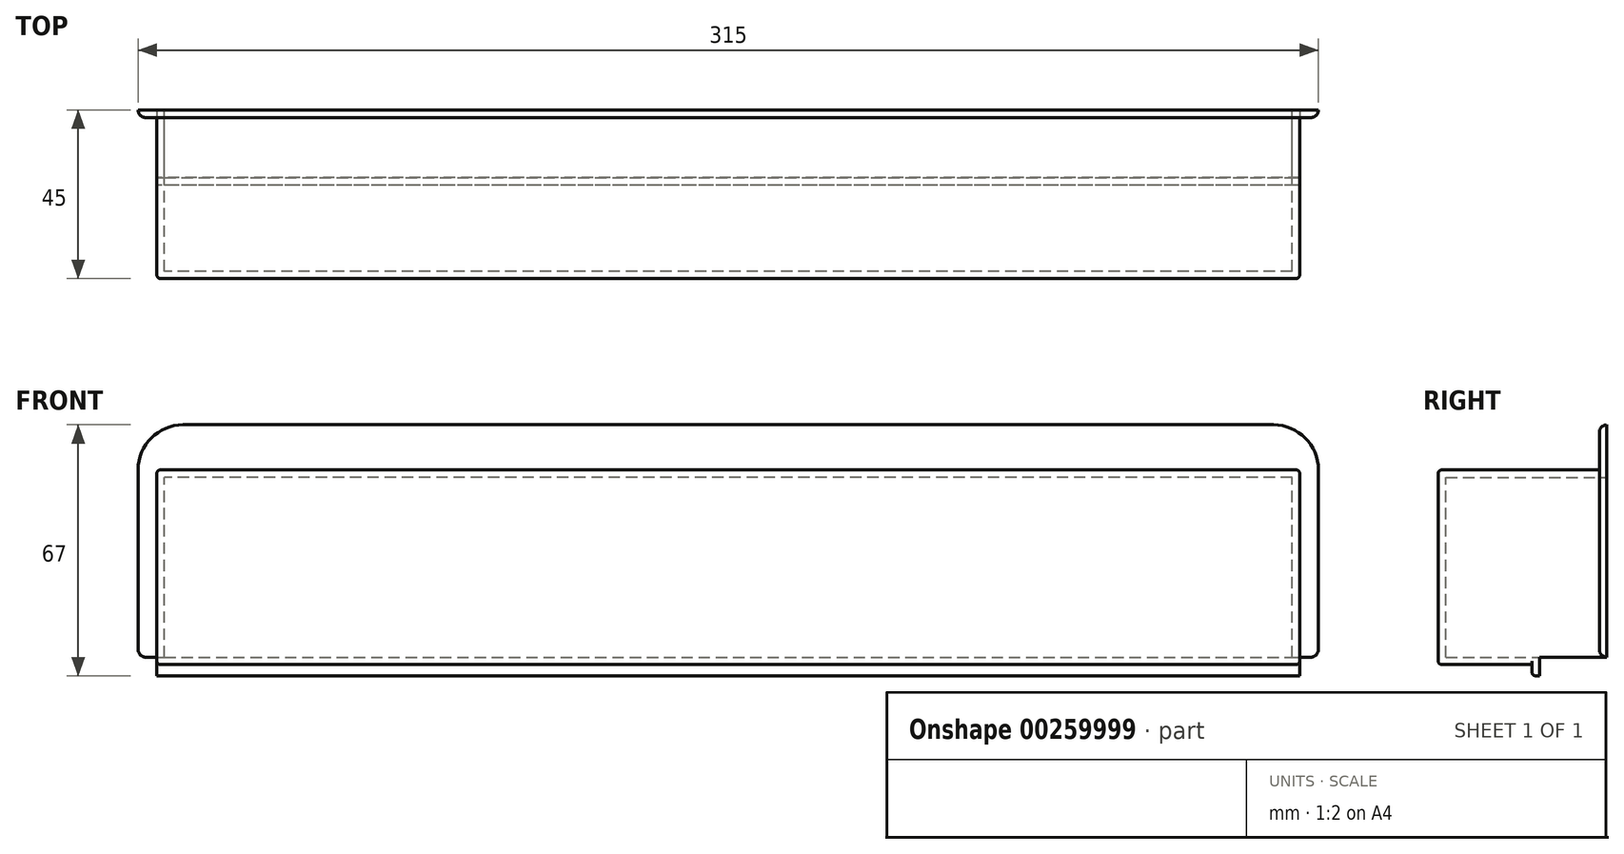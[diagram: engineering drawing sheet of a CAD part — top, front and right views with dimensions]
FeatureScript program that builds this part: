
annotation { "Feature Type Name" : "Feature", "Feature Type Description" : "" }
export const myFeature = defineFeature(function(context is Context, id is Id, definition is map)
    precondition{}
    {
        {
            var Q0;
            Q0=qCreatedBy(makeId("Front.planeOp"),FACE);
            cPlane(context, id + "F0", {"entities" : qUnion([Q0]), "cplaneType" : CPlaneType.OFFSET, "offset" : 15 * mm, "width" : 150 * mm, "height" : 150 * mm});
        }
        {
            var Q0;
            Q0=qCreatedBy(id+"F0.planeOp",FACE);
            var sketch = newSketch(context, id + "F1", { "sketchPlane" : qUnion([Q0])});
            skLineSegment(sketch, "E0.bottom", {"start": v(152.5, -26) * mm, "end": v(-152.5, -26) * mm});
            skLineSegment(sketch, "E0.top", {"start": v(152.5, 26) * mm, "end": v(-152.5, 26) * mm});
            skLineSegment(sketch, "E0.left", {"start": v(152.5, -26) * mm, "end": v(152.5, 26) * mm});
            skLineSegment(sketch, "E0.right", {"start": v(-152.5, -26) * mm, "end": v(-152.5, 26) * mm});
            skPoint(sketch, "E0.middle", {"position": v(0, 0) * mm});
            skLineSegment(sketch, "E1.bottom", {"start": v(150.5, -24) * mm, "end": v(-150.5, -24) * mm});
            skLineSegment(sketch, "E1.top", {"start": v(150.5, 24) * mm, "end": v(-150.5, 24) * mm});
            skLineSegment(sketch, "E1.left", {"start": v(150.5, -24) * mm, "end": v(150.5, 24) * mm});
            skLineSegment(sketch, "E1.right", {"start": v(-150.5, -24) * mm, "end": v(-150.5, 24) * mm});
            skLineSegment(sketch, "E2.top", {"start": v(152.5, 38) * mm, "end": v(-152.5, 38) * mm});
            skLineSegment(sketch, "E2.left", {"start": v(152.5, 26) * mm, "end": v(152.5, 38) * mm});
            skLineSegment(sketch, "E2.right", {"start": v(-152.5, 26) * mm, "end": v(-152.5, 38) * mm});
            skLineSegment(sketch, "E3.left", {"start": v(152.5, -26) * mm, "end": v(152.5, -26) * mm});
            skLineSegment(sketch, "E3.right", {"start": v(-152.5, -26) * mm, "end": v(-152.5, -26) * mm});
            skLineSegment(sketch, "E4.bottom", {"start": v(-152.5, 38) * mm, "end": v(-157.5, 38) * mm});
            skLineSegment(sketch, "E4.left", {"start": v(-152.5, 38) * mm, "end": v(-152.5, -26) * mm});
            skLineSegment(sketch, "E4.right", {"start": v(-157.5, 38) * mm, "end": v(-157.5, -24) * mm});
            skLineSegment(sketch, "E5.left", {"start": v(152.5, 38) * mm, "end": v(152.5, -26) * mm});
            skLineSegment(sketch, "E5.right", {"start": v(157.5, 38) * mm, "end": v(157.5, -24) * mm});
            skLineSegment(sketch, "E6", {"start": v(150.5, -24) * mm, "end": v(152.5, -24) * mm});
            skLineSegment(sketch, "E7", {"start": v(-150.5, -24) * mm, "end": v(-152.5, -24) * mm});
            skLineSegment(sketch, "E8", {"start": v(152.5, -24) * mm, "end": v(157.5, -24) * mm});
            skLineSegment(sketch, "E9", {"start": v(-152.5, -24) * mm, "end": v(-157.5, -24) * mm});
            skLineSegment(sketch, "E10", {"start": v(157.5, 38) * mm, "end": v(157.5, 38) * mm});
            skLineSegment(sketch, "E11", {"start": v(157.5, 38) * mm, "end": v(152.5, 38) * mm});
            skSolve(sketch);
        }
        {
            var Q0;
            Q0=makeQuery(id+"F1.imprint","IMPRINT",FACE,{"disambiguationData":[TD([[makeQuery(id+"F1.imprint","IMPRINT",EDGE,{"derivedFrom":sQuery(id+"F1.wireOp",EDGE,"E1.bottom")}),1.0]])]});
            var Q1;
            Q1=makeQuery(id+"F1.imprint","IMPRINT",FACE,{"disambiguationData":[TD([[makeQuery(id+"F1.imprint","IMPRINT",EDGE,{"derivedFrom":sQuery(id+"F1.wireOp",EDGE,"E1.top")}),-1.0]])]});
            extrude(context, id + "F2", {"entities" : qUnion([Q0, Q1]), "depth" : 45 * mm});
        }
        {
            var Q0;
            {var subQ0=sQuery(id+"F1.wireOp",EDGE,"E0.top");Q0=makeQuery(id+"F1.imprint","IMPRINT",FACE,{"disambiguationData":[TD([[makeQuery(id+"F1.imprint","IMPRINT",EDGE,{"derivedFrom":subQ0}),-1.0]])]});}
            var Q1;
            {var subQ4=sQuery(id+"F1.wireOp",EDGE,"E4.bottom");Q1=makeQuery(id+"F1.imprint","IMPRINT",FACE,{"disambiguationData":[TD([[makeQuery(id+"F1.imprint","IMPRINT",EDGE,{"derivedFrom":subQ4}),1.0]])]});}
            var Q2;
            {var subQ0=sQuery(id+"F1.wireOp",EDGE,"E0.bottom");Q2=makeQuery(id+"F1.imprint","IMPRINT",FACE,{"disambiguationData":[TD([[makeQuery(id+"F1.imprint","IMPRINT",EDGE,{"derivedFrom":subQ0}),1.0]])]});}
            var Q3;
            {var subQ3=sQuery(id+"F1.wireOp",EDGE,"E5.bottom");Q3=makeQuery(id+"F1.imprint","IMPRINT",FACE,{"disambiguationData":[TD([[makeQuery(id+"F1.imprint","IMPRINT",EDGE,{"derivedFrom":subQ3}),-1.0]])]});}
            extrude(context, id + "F3", {"entities" : qUnion([Q0, Q1, Q2, Q3]), "operationType" : NewBodyOperationType.ADD, "depth" : 2 * mm});
        }
        {
            var Q0;
            Q0=makeQuery(id+"F1.imprint","IMPRINT",FACE,{"disambiguationData":[TD([[makeQuery(id+"F1.imprint","IMPRINT",EDGE,{"derivedFrom":sQuery(id+"F1.wireOp",EDGE,"E1.bottom")}),-1.0]])]});
            extrude(context, id + "F4", {"entities" : qUnion([Q0]), "operationType" : NewBodyOperationType.ADD, "depth" : 45 * mm});
        }
        {
            var Q0;
            Q0=makeQuery(id+"F1.imprint","IMPRINT",FACE,{"disambiguationData":[TD([[makeQuery(id+"F1.imprint","IMPRINT",EDGE,{"derivedFrom":sQuery(id+"F1.wireOp",EDGE,"E1.bottom")}),-1.0]])]});
            extrude(context, id + "F5", {"entities" : qUnion([Q0]), "operationType" : NewBodyOperationType.REMOVE, "depth" : 43 * mm});
        }
        {
            var Q0;
            Q0=makeQuery(id+"F3.opExtrude","SWEPT_EDGE",EDGE,{"disambiguationData":[OSD([sQuery(id+"F1.wireOp",EDGE,"E4.bottom"),sQuery(id+"F1.wireOp",EDGE,"E4.right")])]});
            var Q1;
            Q1=makeQuery(id+"FlA18t3Lp9otsd1_1.opFillet","BLEND_EDGE",EDGE,{"blendedFrom":[makeQuery(id+"F3.opExtrude","CAP_EDGE",EDGE,{"disambiguationData":[OSD([sQuery(id+"F1.wireOp",EDGE,"E2.top"),sQuery(id+"F1.wireOp",EDGE,"E4.bottom"),sQuery(id+"F1.wireOp",EDGE,"E5.bottom")])],"isStart":false}),makeQuery(id+"F3.opExtrude","CAP_EDGE",EDGE,{"disambiguationData":[OSD([sQuery(id+"F1.wireOp",EDGE,"E5.right")])],"isStart":false})],"blendedInto":[]});
            fillet(context, id + "F6", {"entities" : qUnion([Q0, Q1]), "radius" : 5 * mm, "tangentPropagation" : true, "allowEdgeOverflow" : false});
        }
        {
            var Q0;
            Q0=makeQuery(id+"F1.imprint","IMPRINT",FACE,{"disambiguationData":[TD([[makeQuery(id+"F1.imprint","IMPRINT",EDGE,{"derivedFrom":sQuery(id+"F1.wireOp",EDGE,"E1.bottom")}),1.0]])]});
            extrude(context, id + "F7", {"entities" : qUnion([Q0]), "operationType" : NewBodyOperationType.REMOVE, "depth" : 20 * mm});
        }
        {
            var Q0;
            Q0=makeQuery(id+"F7.boolean.opBoolean","COPY",FACE,{"derivedFrom":makeQuery(id+"F7.opExtrude","CAP_FACE",FACE,{"disambiguationData":[OSD([sQuery(id+"F1.wireOp",EDGE,"E1.bottom"),sQuery(id+"F1.wireOp",EDGE,"E0.bottom"),sQuery(id+"F1.wireOp",EDGE,"E4.left"),sQuery(id+"F1.wireOp",EDGE,"E5.left"),sQuery(id+"F1.wireOp",EDGE,"E6"),sQuery(id+"F1.wireOp",EDGE,"E7")])],"isStart":false})});
            var sketch = newSketch(context, id + "F8", { "sketchPlane" : qUnion([Q0])});
            skLineSegment(sketch, "E12.bottom", {"start": v(-152.5, -24) * mm, "end": v(152.5, -24) * mm});
            skLineSegment(sketch, "E12.top", {"start": v(-152.5, -29) * mm, "end": v(152.5, -29) * mm});
            skLineSegment(sketch, "E12.left", {"start": v(-152.5, -24) * mm, "end": v(-152.5, -29) * mm});
            skLineSegment(sketch, "E12.right", {"start": v(152.5, -24) * mm, "end": v(152.5, -29) * mm});
            skSolve(sketch);
        }
        {
            var Q0;
            Q0 = qSketchRegion(id + "F8", true);
            extrude(context, id + "F9", {"entities" : qUnion([Q0]), "operationType" : NewBodyOperationType.ADD, "depth" : 2 * mm});
        }
        {
            var Q0;
            {var subQ0=sQuery(id+"F1.wireOp",EDGE,"E5.left");Q0=makeQuery(id+"F7.boolean.opBoolean","MERGE",EDGE,{"derivedFrom":[makeQuery(id+"FlA18t3Lp9otsd1_1.opFillet","BLEND_EDGE",EDGE,{"blendedFrom":[makeQuery(id+"F2.opExtrude","SWEPT_EDGE",EDGE,{"disambiguationData":[OSD([sQuery(id+"F1.wireOp",EDGE,"E0.bottom"),sQuery(id+"F1.wireOp",EDGE,"E5.top"),subQ0])]}),makeQuery(id+"F2.opExtrude","SWEPT_FACE",FACE,{"disambiguationData":[OSD([subQ0])]})],"blendedInto":[makeQuery(id+"F2.opExtrude","SWEPT_FACE",FACE,{"disambiguationData":[OSD([subQ0])]})]}),makeQuery(id+"F7.opExtrude","SWEPT_EDGE",EDGE,{"disambiguationData":[OSD([subQ0,sQuery(id+"F1.wireOp",EDGE,"E6")])]})]});}
            var Q1;
            Q1=makeQuery(id+"F9.opExtrude","CAP_EDGE",EDGE,{"disambiguationData":[OSD([sQuery(id+"F8.wireOp",EDGE,"E12.top")])],"isStart":true});
            var Q2;
            {var subQ0=sQuery(id+"F1.wireOp",EDGE,"E4.left");Q2=makeQuery(id+"F7.boolean.opBoolean","MERGE",EDGE,{"derivedFrom":[makeQuery(id+"FlA18t3Lp9otsd1_1.opFillet","BLEND_EDGE",EDGE,{"blendedFrom":[makeQuery(id+"F2.opExtrude","SWEPT_EDGE",EDGE,{"disambiguationData":[OSD([sQuery(id+"F1.wireOp",EDGE,"E0.bottom"),sQuery(id+"F1.wireOp",EDGE,"E4.top"),subQ0])]}),makeQuery(id+"F2.opExtrude","SWEPT_FACE",FACE,{"disambiguationData":[OSD([subQ0])]})],"blendedInto":[makeQuery(id+"F2.opExtrude","SWEPT_FACE",FACE,{"disambiguationData":[OSD([subQ0])]})]}),makeQuery(id+"F7.opExtrude","SWEPT_EDGE",EDGE,{"disambiguationData":[OSD([subQ0,sQuery(id+"F1.wireOp",EDGE,"E7")])]})]});}
            var Q3;
            Q3=makeQuery(id+"F7.boolean.opBoolean","COPY",EDGE,{"derivedFrom":makeQuery(id+"F7.opExtrude","CAP_EDGE",EDGE,{"disambiguationData":[OSD([sQuery(id+"F1.wireOp",EDGE,"E0.bottom")])],"isStart":false})});
            fillet(context, id + "F10", {"entities" : qUnion([Q0, Q1, Q2, Q3]), "radius" : 1 * mm, "tangentPropagation" : true, "allowEdgeOverflow" : false});
        }
        {
            var Q0;
            Q0=makeQuery(id+"F2.opExtrude","SWEPT_EDGE",EDGE,{"disambiguationData":[OSD([sQuery(id+"F1.wireOp",EDGE,"E0.top"),sQuery(id+"F1.wireOp",EDGE,"E5.left")])]});
            var Q1;
            Q1=makeQuery(id+"F2.opExtrude","CAP_EDGE",EDGE,{"disambiguationData":[OSD([sQuery(id+"F1.wireOp",EDGE,"E5.left")])],"isStart":false});
            var Q2;
            Q2=makeQuery(id+"F2.opExtrude","SWEPT_EDGE",EDGE,{"disambiguationData":[OSD([sQuery(id+"F1.wireOp",EDGE,"E0.bottom"),sQuery(id+"F1.wireOp",EDGE,"E5.left")])]});
            var Q3;
            Q3=makeQuery(id+"F7.boolean.opBoolean","COPY",EDGE,{"derivedFrom":makeQuery(id+"F7.opExtrude","SWEPT_EDGE",EDGE,{"disambiguationData":[OSD([sQuery(id+"F1.wireOp",EDGE,"E5.left"),sQuery(id+"F1.wireOp",EDGE,"E6"),sQuery(id+"F1.wireOp",EDGE,"E8")])]})});
            var Q4;
            Q4=makeQuery(id+"F7.boolean.opBoolean","COPY",EDGE,{"derivedFrom":makeQuery(id+"F7.opExtrude","SWEPT_EDGE",EDGE,{"disambiguationData":[OSD([sQuery(id+"F1.wireOp",EDGE,"E4.left"),sQuery(id+"F1.wireOp",EDGE,"E7"),sQuery(id+"F1.wireOp",EDGE,"E9")])]})});
            var Q5;
            Q5=makeQuery(id+"F2.opExtrude","SWEPT_EDGE",EDGE,{"disambiguationData":[OSD([sQuery(id+"F1.wireOp",EDGE,"E0.bottom"),sQuery(id+"F1.wireOp",EDGE,"E4.left")])]});
            var Q6;
            Q6=makeQuery(id+"F2.opExtrude","CAP_EDGE",EDGE,{"disambiguationData":[OSD([sQuery(id+"F1.wireOp",EDGE,"E4.left")])],"isStart":false});
            var Q7;
            Q7=makeQuery(id+"F2.opExtrude","SWEPT_EDGE",EDGE,{"disambiguationData":[OSD([sQuery(id+"F1.wireOp",EDGE,"E0.top"),sQuery(id+"F1.wireOp",EDGE,"E4.left")])]});
            fillet(context, id + "F11", {"entities" : qUnion([Q0, Q1, Q2, Q3, Q4, Q5, Q6, Q7]), "radius" : 1 * mm, "tangentPropagation" : true, "allowEdgeOverflow" : false});
        }
        {
            var Q0;
            Q0=makeQuery(id+"F2.opExtrude","CAP_EDGE",EDGE,{"disambiguationData":[OSD([sQuery(id+"F1.wireOp",EDGE,"E0.top")])],"isStart":false});
            var Q1;
            Q1=makeQuery(id+"F2.opExtrude","CAP_EDGE",EDGE,{"disambiguationData":[OSD([sQuery(id+"F1.wireOp",EDGE,"E0.bottom")])],"isStart":false});
            var Q2;
            Q2=makeQuery(id+"F3.opExtrude","CAP_EDGE",EDGE,{"disambiguationData":[OSD([sQuery(id+"F1.wireOp",EDGE,"E4.right")])],"isStart":false});
            var Q3;
            {var subQ0=sQuery(id+"F1.wireOp",EDGE,"E4.right");var subQ1=sQuery(id+"F1.wireOp",EDGE,"E4.bottom");Q3=makeQuery(id+"F6.opFillet","BLEND_EDGE",EDGE,{"blendedFrom":[makeQuery(id+"F3.opExtrude","SWEPT_EDGE",EDGE,{"disambiguationData":[OSD([subQ1,subQ0])]}),makeQuery(id+"F3.opExtrude","CAP_FACE",FACE,{"disambiguationData":[OSD([sQuery(id+"F1.wireOp",EDGE,"E0.top"),sQuery(id+"F1.wireOp",EDGE,"E2.top"),subQ1,sQuery(id+"F1.wireOp",EDGE,"E4.left"),subQ0,sQuery(id+"F1.wireOp",EDGE,"E5.bottom"),sQuery(id+"F1.wireOp",EDGE,"E5.left"),sQuery(id+"F1.wireOp",EDGE,"E5.right"),sQuery(id+"F1.wireOp",EDGE,"E8"),sQuery(id+"F1.wireOp",EDGE,"E9")])],"isStart":false})],"blendedInto":[makeQuery(id+"F3.opExtrude","CAP_FACE",FACE,{"disambiguationData":[OSD([sQuery(id+"F1.wireOp",EDGE,"E0.top"),sQuery(id+"F1.wireOp",EDGE,"E2.top"),subQ1,sQuery(id+"F1.wireOp",EDGE,"E4.left"),subQ0,sQuery(id+"F1.wireOp",EDGE,"E5.bottom"),sQuery(id+"F1.wireOp",EDGE,"E5.left"),sQuery(id+"F1.wireOp",EDGE,"E5.right"),sQuery(id+"F1.wireOp",EDGE,"E8"),sQuery(id+"F1.wireOp",EDGE,"E9")])],"isStart":false})]});}
            var Q4;
            Q4=makeQuery(id+"F3.opExtrude","CAP_EDGE",EDGE,{"disambiguationData":[OSD([sQuery(id+"F1.wireOp",EDGE,"E2.top"),sQuery(id+"F1.wireOp",EDGE,"E4.bottom"),sQuery(id+"F1.wireOp",EDGE,"E5.bottom")])],"isStart":false});
            fillet(context, id + "F12", {"entities" : qUnion([Q0, Q1, Q2, Q3, Q4]), "radius" : 1 * mm, "tangentPropagation" : true, "allowEdgeOverflow" : false});
        }
        {
            var Q0;
            {var subQ3=sQuery(id+"F1.wireOp",EDGE,"E4.bottom");Q0=makeQuery(id+"F1.imprint","IMPRINT",FACE,{"disambiguationData":[TD([[makeQuery(id+"F1.imprint","IMPRINT",EDGE,{"derivedFrom":subQ3}),1.0]])]});}
            var Q1;
            {var subQ0=sQuery(id+"F1.wireOp",EDGE,"E0.top");Q1=makeQuery(id+"F1.imprint","IMPRINT",FACE,{"disambiguationData":[TD([[makeQuery(id+"F1.imprint","IMPRINT",EDGE,{"derivedFrom":subQ0}),-1.0]])]});}
            var Q2;
            Q2=makeQuery(id+"F1.imprint","IMPRINT",FACE,{"disambiguationData":[TD([[makeQuery(id+"F1.imprint","IMPRINT",EDGE,{"derivedFrom":sQuery(id+"F1.wireOp",EDGE,"E1.top")}),-1.0]])]});
            var Q3;
            Q3=makeQuery(id+"F1.imprint","IMPRINT",FACE,{"disambiguationData":[TD([[makeQuery(id+"F1.imprint","IMPRINT",EDGE,{"derivedFrom":sQuery(id+"F1.wireOp",EDGE,"E5.right")}),-1.0]])]});
            extrude(context, id + "F13", {"entities" : qUnion([Q0, Q1, Q2, Q3]), "operationType" : NewBodyOperationType.ADD, "depth" : 2 * mm});
        }
        {
            var Q0;
            Q0=makeQuery(id+"F13.opExtrude","SWEPT_EDGE",EDGE,{"disambiguationData":[OSD([sQuery(id+"F1.wireOp",EDGE,"E5.right"),sQuery(id+"F1.wireOp",EDGE,"E11")])]});
            var Q1;
            Q1=makeQuery(id+"F13.opExtrude","SWEPT_EDGE",EDGE,{"disambiguationData":[OSD([sQuery(id+"F1.wireOp",EDGE,"E4.bottom"),sQuery(id+"F1.wireOp",EDGE,"E4.right")])]});
            fillet(context, id + "F14", {"entities" : qUnion([Q0, Q1]), "radius" : 12 * mm, "tangentPropagation" : true, "allowEdgeOverflow" : false});
        }
        {
            var Q0;
            Q0=makeQuery(id+"F13.opExtrude","CAP_EDGE",EDGE,{"disambiguationData":[OSD([sQuery(id+"F1.wireOp",EDGE,"E5.right")])],"isStart":false});
            fillet(context, id + "F15", {"entities" : qUnion([Q0]), "radius" : 2 * mm, "tangentPropagation" : true, "allowEdgeOverflow" : false});
        }
        {
            var Q0;
            {var subQ0=sQuery(id+"F1.wireOp",EDGE,"E6");Q0=makeQuery(id+"F15.opFillet","BLEND_EDGE",EDGE,{"blendedFrom":[makeQuery(id+"F13.opExtrude","CAP_EDGE",EDGE,{"disambiguationData":[OSD([sQuery(id+"F1.wireOp",EDGE,"E5.right")])],"isStart":false}),makeQuery(id+"F13.boolean.opBoolean","MERGE",FACE,{"derivedFrom":[makeQuery(id+"F7.boolean.opBoolean","COPY",FACE,{"derivedFrom":makeQuery(id+"F7.opExtrude","SWEPT_FACE",FACE,{"disambiguationData":[OSD([sQuery(id+"F1.wireOp",EDGE,"E1.bottom"),subQ0,sQuery(id+"F1.wireOp",EDGE,"E7")])]})}),makeQuery(id+"F13.opExtrude","SWEPT_FACE",FACE,{"disambiguationData":[OSD([subQ0,sQuery(id+"F1.wireOp",EDGE,"E8")])]})]})],"blendedInto":[makeQuery(id+"F13.boolean.opBoolean","MERGE",FACE,{"derivedFrom":[makeQuery(id+"F7.boolean.opBoolean","COPY",FACE,{"derivedFrom":makeQuery(id+"F7.opExtrude","SWEPT_FACE",FACE,{"disambiguationData":[OSD([sQuery(id+"F1.wireOp",EDGE,"E1.bottom"),subQ0,sQuery(id+"F1.wireOp",EDGE,"E7")])]})}),makeQuery(id+"F13.opExtrude","SWEPT_FACE",FACE,{"disambiguationData":[OSD([subQ0,sQuery(id+"F1.wireOp",EDGE,"E8")])]})]})]});}
            var Q1;
            {var subQ0=sQuery(id+"F1.wireOp",EDGE,"E9");var subQ1=sQuery(id+"F1.wireOp",EDGE,"E7");Q1=makeQuery(id+"F15.opFillet","BLEND_EDGE",EDGE,{"blendedFrom":[makeQuery(id+"F13.opExtrude","CAP_EDGE",EDGE,{"disambiguationData":[OSD([sQuery(id+"F1.wireOp",EDGE,"E4.right")])],"isStart":false}),makeQuery(id+"F13.boolean.opBoolean","MERGE",FACE,{"derivedFrom":[makeQuery(id+"F7.boolean.opBoolean","MERGE",FACE,{"derivedFrom":[makeQuery(id+"F3.opExtrude","SWEPT_FACE",FACE,{"disambiguationData":[OSD([subQ0])]}),makeQuery(id+"F7.opExtrude","SWEPT_FACE",FACE,{"disambiguationData":[OSD([sQuery(id+"F1.wireOp",EDGE,"E1.bottom"),sQuery(id+"F1.wireOp",EDGE,"E6"),subQ1])]})]}),makeQuery(id+"F13.opExtrude","SWEPT_FACE",FACE,{"disambiguationData":[OSD([subQ1,subQ0])]})]})],"blendedInto":[makeQuery(id+"F13.boolean.opBoolean","MERGE",FACE,{"derivedFrom":[makeQuery(id+"F7.boolean.opBoolean","MERGE",FACE,{"derivedFrom":[makeQuery(id+"F3.opExtrude","SWEPT_FACE",FACE,{"disambiguationData":[OSD([subQ0])]}),makeQuery(id+"F7.opExtrude","SWEPT_FACE",FACE,{"disambiguationData":[OSD([sQuery(id+"F1.wireOp",EDGE,"E1.bottom"),sQuery(id+"F1.wireOp",EDGE,"E6"),subQ1])]})]}),makeQuery(id+"F13.opExtrude","SWEPT_FACE",FACE,{"disambiguationData":[OSD([subQ1,subQ0])]})]})]});}
            fillet(context, id + "F16", {"entities" : qUnion([Q0, Q1]), "radius" : 2 * mm, "tangentPropagation" : true, "allowEdgeOverflow" : false});
        }
    });
